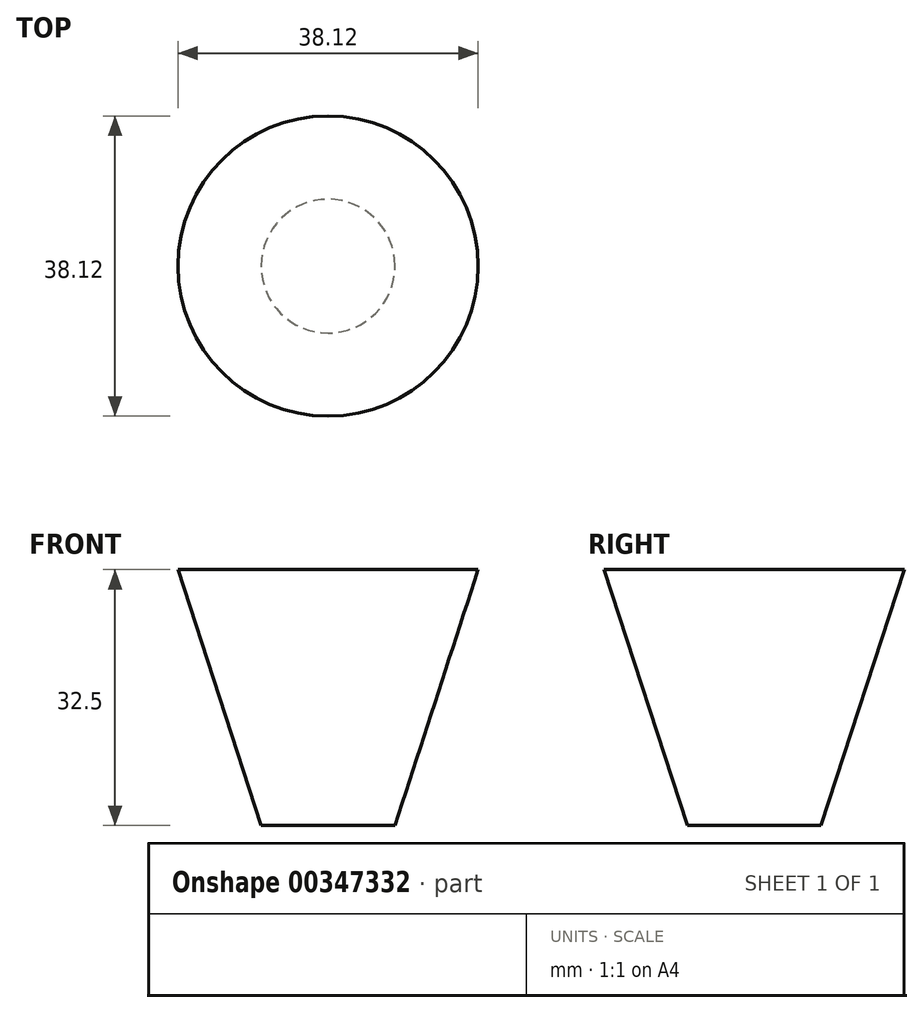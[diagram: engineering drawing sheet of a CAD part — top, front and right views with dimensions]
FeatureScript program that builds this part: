
annotation { "Feature Type Name" : "Feature", "Feature Type Description" : "" }
export const myFeature = defineFeature(function(context is Context, id is Id, definition is map)
    precondition{}
    {
        {
            var Q0;
            Q0=qCreatedBy(makeId("Top.planeOp"),FACE);
            var sketch = newSketch(context, id + "F0", { "sketchPlane" : qUnion([Q0])});
            skCircle(sketch, "E0", {"center": v(0, 0) * mm, "radius": 8.5 * mm});
            skSolve(sketch);
        }
        {
            var Q0;
            Q0 = qSketchRegion(id + "F0", true);
            extrude(context, id + "F1", {"entities" : qUnion([Q0]), "depth" : 32.5 * mm, "hasDraft" : true, "draftAngle" : 18 * degree});
        }
    });
